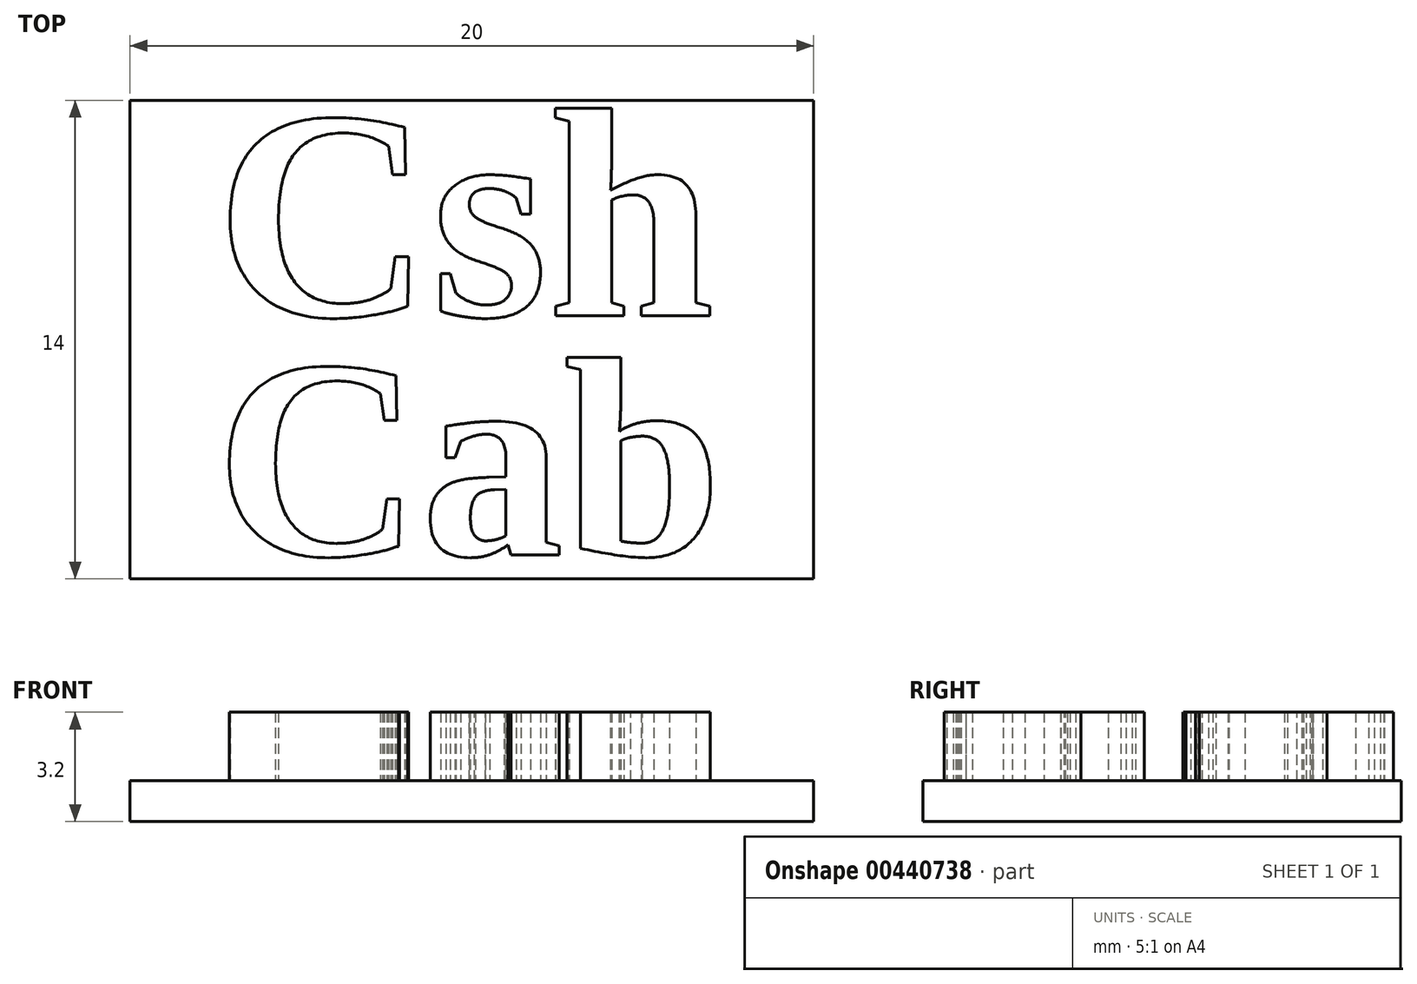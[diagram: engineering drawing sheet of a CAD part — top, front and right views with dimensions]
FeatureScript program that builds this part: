
annotation { "Feature Type Name" : "Feature", "Feature Type Description" : "" }
export const myFeature = defineFeature(function(context is Context, id is Id, definition is map)
    precondition{}
    {
        {
            var Q0;
            Q0=qCreatedBy(makeId("Top.planeOp"),FACE);
            var sketch = newSketch(context, id + "F0", { "sketchPlane" : qUnion([Q0])});
            skLineSegment(sketch, "E0.bottom", {"start": v(10, 7) * mm, "end": v(-10, 7) * mm});
            skLineSegment(sketch, "E0.top", {"start": v(10, -7) * mm, "end": v(-10, -7) * mm});
            skLineSegment(sketch, "E0.left", {"start": v(10, 7) * mm, "end": v(10, -7) * mm});
            skLineSegment(sketch, "E0.right", {"start": v(-10, 7) * mm, "end": v(-10, -7) * mm});
            skPoint(sketch, "E0.middle", {"position": v(0, 0) * mm});
            skSolve(sketch);
        }
        {
            var Q0;
            Q0 = qSketchRegion(id + "F0", true);
            extrude(context, id + "F1", {"entities" : qUnion([Q0]), "depth" : 1.2 * mm});
        }
        {
            var Q0;
            Q0=makeQuery(id+"F1.opExtrude","CAP_FACE",FACE,{"disambiguationData":[OSD([sQuery(id+"F0.wireOp",EDGE,"E0.bottom"),sQuery(id+"F0.wireOp",EDGE,"E0.top"),sQuery(id+"F0.wireOp",EDGE,"E0.left"),sQuery(id+"F0.wireOp",EDGE,"E0.right")])],"isStart":false});
            var sketch = newSketch(context, id + "F2", { "sketchPlane" : qUnion([Q0])});
            skText(sketch, "E1", { "text": "Csh", "fontName": "Tinos-Bold.ttf"});
            const initialGuessF2  = {"E1": [-0.0075, 0.0007, 1, 0, 0.0063]};
            skSetInitialGuess(sketch, initialGuessF2);
            skSolve(sketch);
        }
        {
            var Q0;
            Q0=makeQuery(id+"F2.imprint","IMPRINT",FACE,{"disambiguationData":[TD([[makeQuery(id+"F2.imprint","IMPRINT",EDGE,{"derivedFrom":sQuery(id+"F2.wireOp",EDGE,"E1.sketch_text.stroke-0")}),1.0]])]});
            var sketch = newSketch(context, id + "F3", { "sketchPlane" : qUnion([Q0])});
            skText(sketch, "E2", { "text": "Cab", "fontName": "Tinos-Bold.ttf"});
            skLineSegment(sketch, "E3.0.0", {"start": v(4.08, 5.03) * mm, "end": v(4.08, 6.77) * mm, "construction": true});
            skLineSegment(sketch, "E3.0.1", {"start": v(4.08, 6.77) * mm, "end": v(2.44, 6.77) * mm, "construction": true});
            skLineSegment(sketch, "E3.0.2", {"start": v(2.44, 6.77) * mm, "end": v(2.44, 6.49) * mm, "construction": true});
            skLineSegment(sketch, "E3.0.3", {"start": v(2.44, 6.49) * mm, "end": v(2.85, 6.39) * mm, "construction": true});
            skLineSegment(sketch, "E3.0.4", {"start": v(2.85, 6.39) * mm, "end": v(2.85, 1.09) * mm, "construction": true});
            skLineSegment(sketch, "E3.0.5", {"start": v(2.85, 1.09) * mm, "end": v(2.46, 0.98) * mm, "construction": true});
            skLineSegment(sketch, "E3.0.6", {"start": v(2.46, 0.98) * mm, "end": v(2.46, 0.7) * mm, "construction": true});
            skLineSegment(sketch, "E3.0.7", {"start": v(2.46, 0.7) * mm, "end": v(4.45, 0.7) * mm, "construction": true});
            skLineSegment(sketch, "E3.0.8", {"start": v(4.45, 0.7) * mm, "end": v(4.45, 0.98) * mm, "construction": true});
            skLineSegment(sketch, "E3.0.9", {"start": v(4.45, 0.98) * mm, "end": v(4.08, 1.09) * mm, "construction": true});
            skLineSegment(sketch, "E3.0.10", {"start": v(4.08, 1.09) * mm, "end": v(4.08, 4.09) * mm, "construction": true});
            skFitSpline(sketch, "E3.0.11", {"points": [v(4.08, 4.09) * mm, v(4.4, 4.23) * mm, v(4.73, 4.23) * mm], "construction": true});
            skFitSpline(sketch, "E3.0.12", {"points": [v(4.73, 4.23) * mm, v(5.01, 4.23) * mm, v(5.17, 4.03) * mm], "construction": true});
            skFitSpline(sketch, "E3.0.13", {"points": [v(5.17, 4.03) * mm, v(5.32, 3.83) * mm, v(5.32, 3.47) * mm], "construction": true});
            skLineSegment(sketch, "E3.0.14", {"start": v(5.32, 3.47) * mm, "end": v(5.32, 1.09) * mm, "construction": true});
            skLineSegment(sketch, "E3.0.15", {"start": v(5.32, 1.09) * mm, "end": v(4.96, 0.98) * mm, "construction": true});
            skLineSegment(sketch, "E3.0.16", {"start": v(4.96, 0.98) * mm, "end": v(4.96, 0.7) * mm, "construction": true});
            skLineSegment(sketch, "E3.0.17", {"start": v(4.96, 0.7) * mm, "end": v(6.95, 0.7) * mm, "construction": true});
            skLineSegment(sketch, "E3.0.18", {"start": v(6.95, 0.7) * mm, "end": v(6.95, 0.98) * mm, "construction": true});
            skLineSegment(sketch, "E3.0.19", {"start": v(6.95, 0.98) * mm, "end": v(6.55, 1.09) * mm, "construction": true});
            skLineSegment(sketch, "E3.0.20", {"start": v(6.55, 1.09) * mm, "end": v(6.55, 3.64) * mm, "construction": true});
            skFitSpline(sketch, "E3.0.21", {"points": [v(6.55, 3.64) * mm, v(6.55, 4.82) * mm, v(5.44, 4.82) * mm], "construction": true});
            skFitSpline(sketch, "E3.0.22", {"points": [v(5.44, 4.82) * mm, v(4.96, 4.82) * mm, v(4.35, 4.52) * mm], "construction": true});
            skLineSegment(sketch, "E3.0.23", {"start": v(4.35, 4.52) * mm, "end": v(4.06, 4.37) * mm, "construction": true});
            skFitSpline(sketch, "E3.0.24", {"points": [v(4.06, 4.37) * mm, v(4.08, 4.75) * mm, v(4.08, 5.03) * mm], "construction": true});
            skLineSegment(sketch, "E4.0", {"start": v(-7.5, 0.7) * mm, "end": v(7.5, 0.7) * mm, "construction": true});
            const initialGuessF3  = {"E2": [-0.0075, -0.0063, 1, 0, 0.006]};
            skSetInitialGuess(sketch, initialGuessF3);
            skSolve(sketch);
        }
        {
            var Q0;
            Q0 = qSketchRegion(id + "F2", true);
            var Q1;
            Q1 = qSketchRegion(id + "F3", true);
            extrude(context, id + "F4", {"entities" : qUnion([Q0, Q1]), "operationType" : NewBodyOperationType.ADD, "depth" : 2 * mm});
        }
    });
